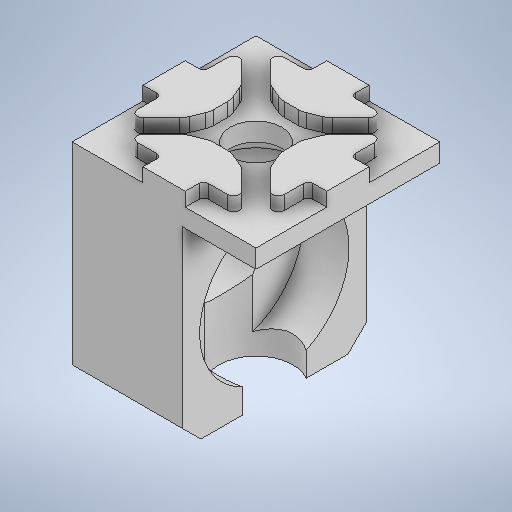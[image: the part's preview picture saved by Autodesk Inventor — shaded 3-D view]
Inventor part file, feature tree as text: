
AUTODESK INVENTOR PART (.ipt)
format: ipt  version: 2025 (Build 290162010, 162A)  size: 479,744 bytes
history: native  units: in
note: dims shown in document units (in); Inventor stores cm internally (conversion verified against a paired STEP export)
features: extrude x7, sketch x7, chamfer x3, fillet x1
ambient origin geometry x8: Origin, YZ Plane, XZ Plane, XY Plane, X Axis, Y Axis, Z Axis, Center Point
bodies: Body1 (feature_tree)
feature tree (18):
  extrude  "Extrusion10"  Depth=0.7874in
  extrude  "Extrusion11"  Depth=0.0787in TaperAngle=0.0deg
  fillet  "Rundung3"  Radius=0.1811in
  extrude  "Extrusion12"  Depth=0.0498in
  extrude  "Extrusion15"  Depth=0.0834in
  extrude  "Extrusion17"  Depth=0.1253in
  extrude  "Extrusion18"  Depth=0.2421in
  chamfer  "Fasen4"  Distance=0.0591in
  extrude  "Extrusion19"  Depth=0.315in TaperAngle=45.0deg
  chamfer  "Fasen5"  Distance=0.0591in
  chamfer  "Fasen6"  Distance=0.4724in
  sketch  "Skizze10"  dims[d78=0.7874in d79=0.7874in]
  sketch  "Skizze11"  dims[d80=0.2205in d81=0.0787in d82=0.0in d83=0.1811in]
  sketch  "Skizze12"  dims[d85=0.0394in d87=0.0498in]
  sketch  "Skizze16"  dims[d89=45.0deg d90=0.0834in]
  sketch  "Skizze19"  dims[d91=45.0deg d92=0.1253in]
  sketch  "Skizze20"  dims[d93=0.0893in d94=0.2421in d95=0.0591in d96=0.0in]
  sketch  "Skizze21"  dims[d97=0.0787in d98=0.1811in d102=45.0deg d104=45.0deg d107=0.2421in d108=0.1811in d112=45.0deg d114=45.0deg d117=0.2421in d118=0.1811in d119=0.0394in d122=45.0deg d124=45.0deg d127=0.2421in d128=0.0591in d129=0.4724in d130=0.8268in d131=0.0in d141=0.315in d142=0.8268in d143=0.0in d147=0.2756in d148=0.3937in d149=0.3937in d150=0.0in d151=0.0in d152=0.6398in d153=0.1969in d154=0.0in d155=0.0787in d156=0.0787in d157=45.0deg d158=0.3642in d159=0.315in d160=0.0in d161=0.0717in d162=0.0787in d163=45.0deg d164=0.0098in d165=0.0787in d166=45.0deg d144=0.0344in]
